# Revit family: Overhead_Door-CHI-Planks-Oversized
name_source: partatom
category: Specialty Equipment
units: mm (PartAtom-declared; Revit-internal decimal feet)

## family parameters
Always vertical = Yes
Cut with Voids When Loaded = No
Enable Cutting in Views = No
Host = Wall
Maintain Annotation Orientation = No
OmniClass Number = 23.30.10.21
OmniClass Title = Special Function Doors
Part Type = Normal
Room Calculation Point = No
Round Connector Dimension = Use Diameter
Shared = No

## types (1)
- Not a Type - Type Catalog
    Air Infiltration = Contact Manufacturer for More Information
    Assembly Code = B2050.10
    C Door Bottom Offset = 0.03'
    C Model = 1
    C OFG = 0.00'
    C Panel Size = 2
    C Side Rail Radius = 1.25'
    Certified Windload = Yes
    Construction Type = Glass garage doors
    DASMA Thermal Verification Program = No
    Default Elevation = 0.00'
    Description = Wood-Look Garage Doors
    Fire Rating = Contact Manufacturer for More Information
    Flame Spread = Contact Manufacturer for More Information
    Glass Finish = Glass - C.H.I Overhead Doors - Frosted
    IECC Compliant = No
    Impact = Yes
    Keynote = 08 30 00
    Load Classification = Other
    Long Panel = Yes
    Manufacturer = C.H.I. Overhead Doors
    Manufacturer Fax Number = 800-738-5006
    Material Disclaimer = Accents Woodtones, when ordered, contain non-repeating patterns. Color discrepancies may appear differently on desktop displays. Contact Manufacturer for Availability of Finishes per Model
    Model = 2327
    Number of Phases = 1
    Number of Poles = 1
    Panel Finish = Metal - Powder Coat - C.H.I Overhead Doors - White
    Product Documentation Link = https://www.chiohd.com
    Product Page URL = https://www.chiohd.com
    R-Value = 10.29
    Short Panel = No
    Steel Gauge = 27
    Thickness = 0.17'
    U Factor = 0.29
    URL = https://www.chiohd.com
    Version = 2021-v1.a
    Voltage = 115 V

## geometry (parser evidence)
native form markers: Sweep x41
no freeform markers — native parametric forms only
